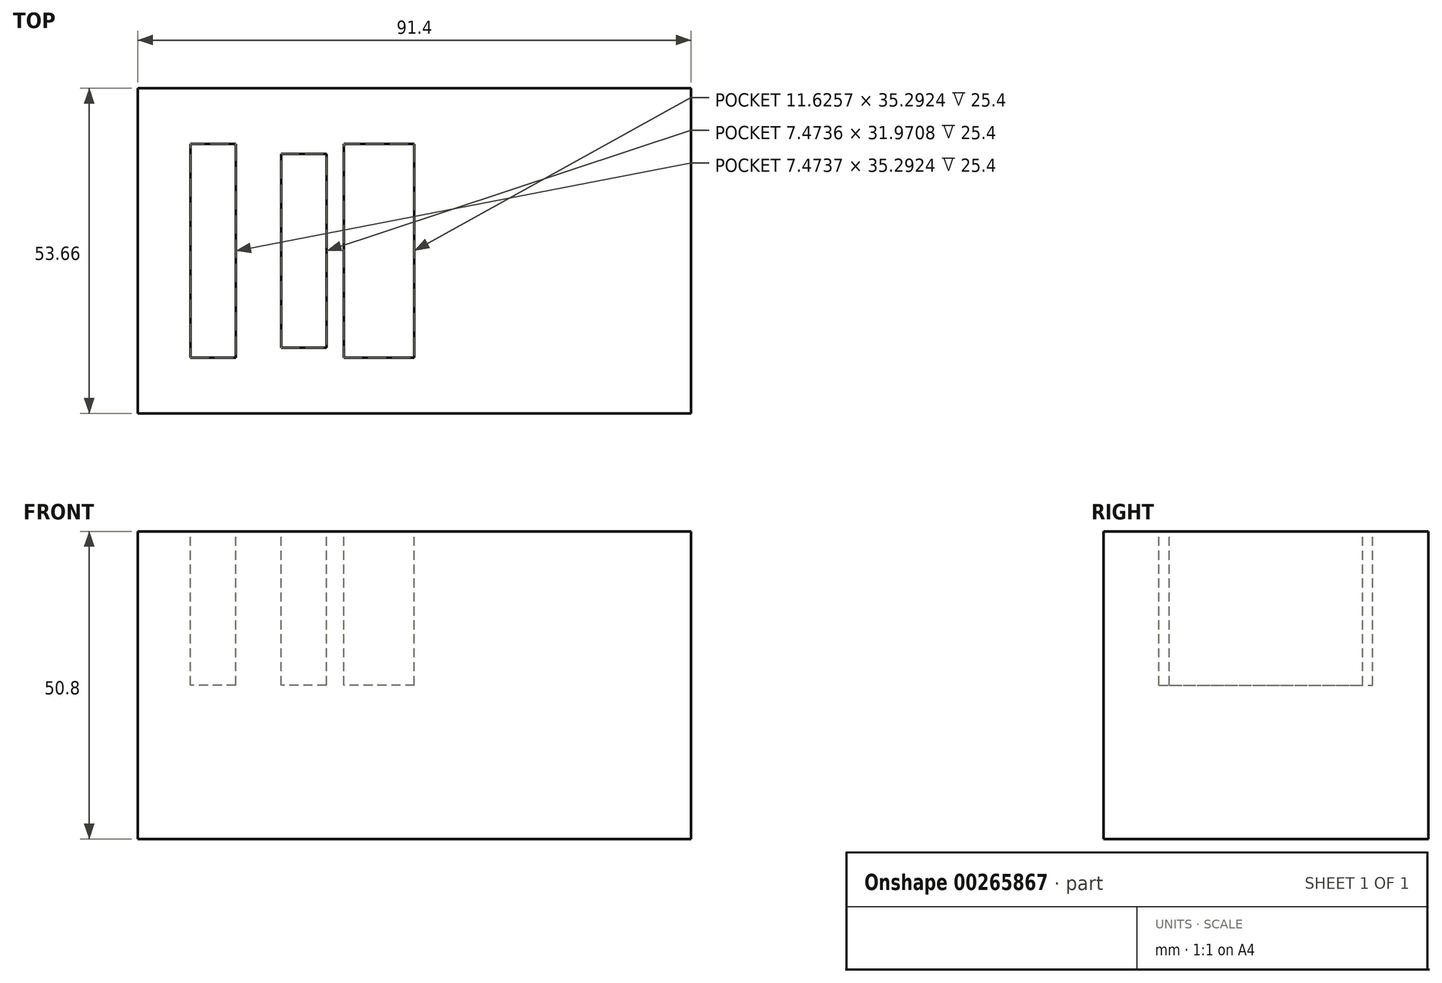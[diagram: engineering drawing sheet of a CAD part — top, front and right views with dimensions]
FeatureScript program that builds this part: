
annotation { "Feature Type Name" : "Feature", "Feature Type Description" : "" }
export const myFeature = defineFeature(function(context is Context, id is Id, definition is map)
    precondition{}
    {
        {
            var Q0;
            Q0=qCreatedBy(makeId("Top.planeOp"),FACE);
            var sketch = newSketch(context, id + "F0", { "sketchPlane" : qUnion([Q0])});
            skLineSegment(sketch, "E0.bottom", {"start": v(45.7, -26.83) * mm, "end": v(-45.7, -26.83) * mm});
            skLineSegment(sketch, "E0.top", {"start": v(45.7, 26.83) * mm, "end": v(-45.7, 26.83) * mm});
            skLineSegment(sketch, "E0.left", {"start": v(45.7, -26.83) * mm, "end": v(45.7, 26.83) * mm});
            skLineSegment(sketch, "E0.right", {"start": v(-45.7, -26.83) * mm, "end": v(-45.7, 26.83) * mm});
            skPoint(sketch, "E0.middle", {"position": v(0, 0) * mm});
            skSolve(sketch);
        }
        {
            var Q0;
            Q0 = qSketchRegion(id + "F0", true);
            extrude(context, id + "F1", {"entities" : qUnion([Q0]), "depth" : 50.8 * mm});
        }
        {
            var Q0;
            Q0=makeQuery(id+"F1.opExtrude","CAP_FACE",FACE,{"disambiguationData":[OSD([sQuery(id+"F0.wireOp",EDGE,"E0.bottom"),sQuery(id+"F0.wireOp",EDGE,"E0.top"),sQuery(id+"F0.wireOp",EDGE,"E0.left"),sQuery(id+"F0.wireOp",EDGE,"E0.right")])],"isStart":false});
            var sketch = newSketch(context, id + "F2", { "sketchPlane" : qUnion([Q0])});
            skLineSegment(sketch, "E1.bottom", {"start": v(-29.48, -17.65) * mm, "end": v(-36.95, -17.65) * mm});
            skLineSegment(sketch, "E1.top", {"start": v(-29.48, 17.65) * mm, "end": v(-36.95, 17.65) * mm});
            skLineSegment(sketch, "E1.left", {"start": v(-29.48, -17.65) * mm, "end": v(-29.48, 17.65) * mm});
            skLineSegment(sketch, "E1.right", {"start": v(-36.95, -17.65) * mm, "end": v(-36.95, 17.65) * mm});
            skPoint(sketch, "E1.middle", {"position": v(-33.22, 0) * mm});
            skLineSegment(sketch, "E2.bottom", {"start": v(-14.53, -15.99) * mm, "end": v(-22, -15.99) * mm});
            skLineSegment(sketch, "E2.top", {"start": v(-14.53, 15.99) * mm, "end": v(-22, 15.99) * mm});
            skLineSegment(sketch, "E2.left", {"start": v(-14.53, -15.99) * mm, "end": v(-14.53, 15.99) * mm});
            skLineSegment(sketch, "E2.right", {"start": v(-22, -15.99) * mm, "end": v(-22, 15.99) * mm});
            skPoint(sketch, "E2.middle", {"position": v(-18.27, 0) * mm});
            skLineSegment(sketch, "E3.bottom", {"start": v(0, -17.65) * mm, "end": v(-11.63, -17.65) * mm});
            skLineSegment(sketch, "E3.top", {"start": v(0, 17.65) * mm, "end": v(-11.63, 17.65) * mm});
            skLineSegment(sketch, "E3.left", {"start": v(0, -17.65) * mm, "end": v(0, 17.65) * mm});
            skLineSegment(sketch, "E3.right", {"start": v(-11.63, -17.65) * mm, "end": v(-11.63, 17.65) * mm});
            skPoint(sketch, "E3.middle", {"position": v(-5.81, 0) * mm});
            skSolve(sketch);
        }
        {
            var Q0;
            Q0 = qSketchRegion(id + "F2", true);
            extrude(context, id + "F3", {"entities" : qUnion([Q0]), "operationType" : NewBodyOperationType.REMOVE, "oppositeDirection" : true, "depth" : 25.4 * mm});
        }
    });
